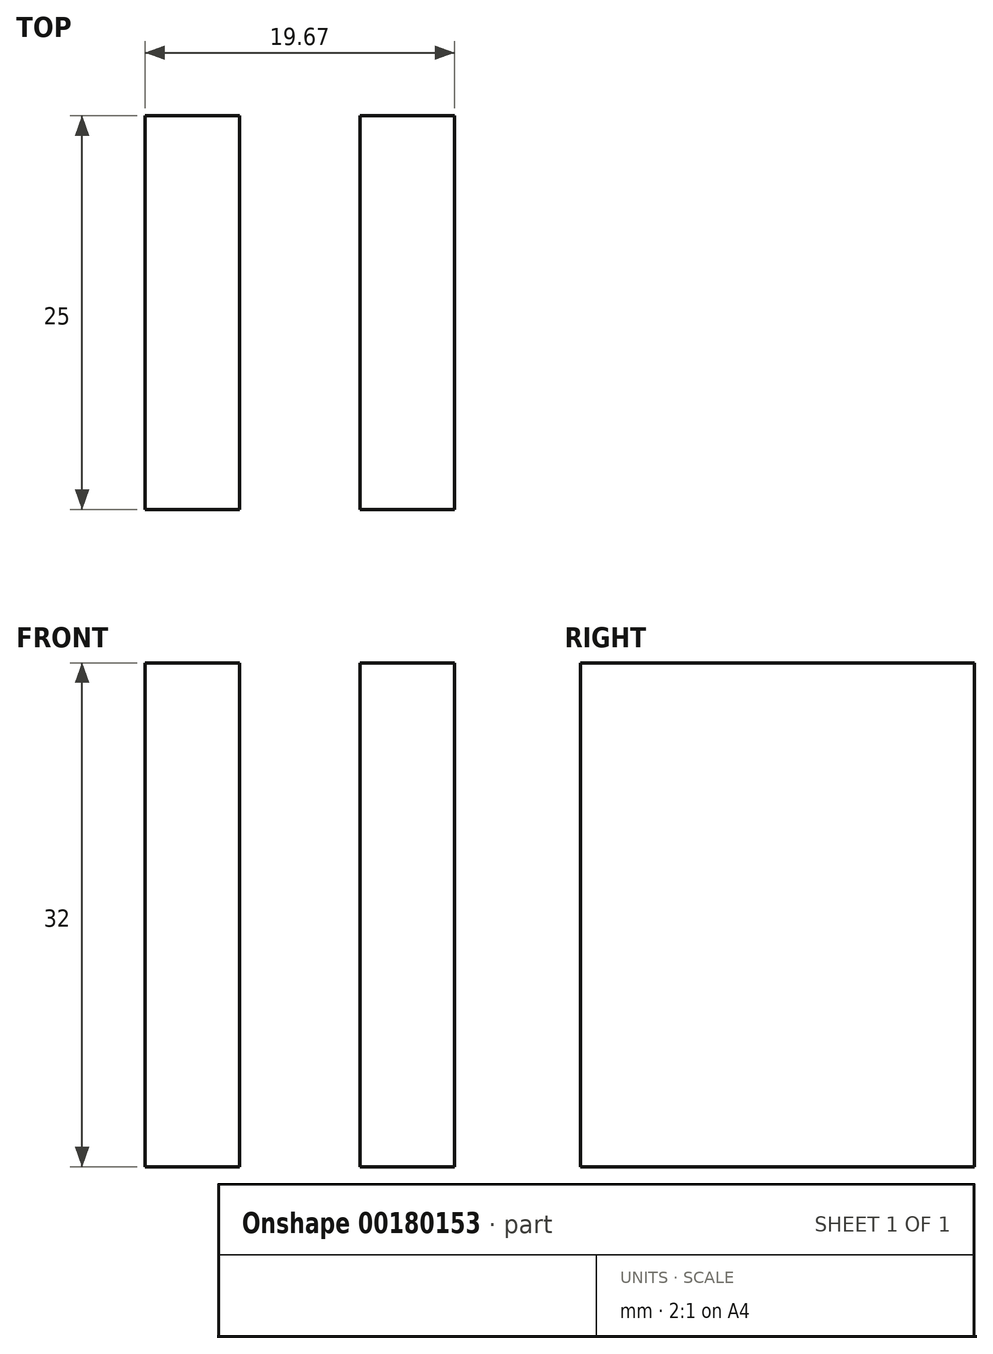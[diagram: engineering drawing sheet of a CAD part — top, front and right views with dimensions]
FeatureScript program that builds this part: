
annotation { "Feature Type Name" : "Feature", "Feature Type Description" : "" }
export const myFeature = defineFeature(function(context is Context, id is Id, definition is map)
    precondition{}
    {
        {
            var Q0;
            Q0=qCreatedBy(makeId("Front.planeOp"),FACE);
            var sketch = newSketch(context, id + "F0", { "sketchPlane" : qUnion([Q0])});
            skLineSegment(sketch, "E0", {"start": v(-46.66, 18.98) * mm, "end": v(-46.66, -13.02) * mm});
            skLineSegment(sketch, "E1", {"start": v(-46.66, -13.02) * mm, "end": v(-40.66, -13.02) * mm});
            skLineSegment(sketch, "E2", {"start": v(-40.66, -13.02) * mm, "end": v(-40.66, 18.98) * mm});
            skLineSegment(sketch, "E3", {"start": v(-40.66, 18.98) * mm, "end": v(-46.66, 18.98) * mm});
            skLineSegment(sketch, "E4", {"start": v(-32.99, 18.98) * mm, "end": v(-32.99, -13.02) * mm});
            skLineSegment(sketch, "E5", {"start": v(-32.99, -13.02) * mm, "end": v(-26.99, -13.02) * mm});
            skLineSegment(sketch, "E6", {"start": v(-26.99, -13.02) * mm, "end": v(-26.99, 18.98) * mm});
            skLineSegment(sketch, "E7", {"start": v(-26.99, 18.98) * mm, "end": v(-32.99, 18.98) * mm});
            skSolve(sketch);
        }
        {
            var Q0;
            Q0 = qSketchRegion(id + "F0", true);
            extrude(context, id + "F1", {"entities" : qUnion([Q0]), "depth" : 25 * mm});
        }
    });
